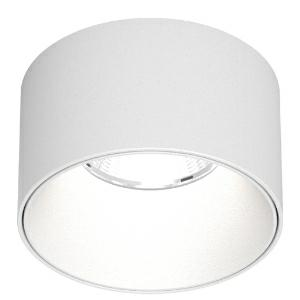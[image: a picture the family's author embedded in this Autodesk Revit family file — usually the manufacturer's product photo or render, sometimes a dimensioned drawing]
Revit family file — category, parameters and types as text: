
# Revit family: invader_semi-on_220-1194
name_source: partatom
category: Lighting Fixtures
units: mm (PartAtom-declared; Revit-internal decimal feet)

## family parameters
Cut with Voids When Loaded = No
Host = Face
Light Source = No
Part Type = Normal
Room Calculation Point = No
Round Connector Dimension = Use Diameter
Shared = No

## types (1)
- 220-1194-H27-W22 (1 x LED, 1043.88 lm, 9.6 W, 2700K)
    Apparent Load = 10 VA
    CIE Flux Codes = 99 100 100 100 67
    Color Rendering = 1A/90…99
    Color Temperature = 2700K
    Default Elevation = 1800 mm
    Description = INVADER SEMI-ON
    Height = 0 mm  [stored 0 ft]
    Lamp = 1 x LED
    Lamp Light Flux = 1043.88 lm
    Lamp Power = 9.6 W
    Lamp count = 1
    Length = 75 mm
    Luminous efficacy = 73 lm/W
    Manufacturer = Prolicht
    ModVariant = No
    Model = 220-1194
    Mounting Place = Ceiling
    Mounting Type = Recessed
    Number of Poles = 1
    OnlyDefault = Yes
    Power Factor = 1
    Product Name = INVADER SEMI-ON
    Product group = Recessed spotlights
    ProductGroupID = 422
    Protection Class = Protection class
    Protection Degree = Degree of protection
    RLX_Detail_Level = 1
    RLX_Emergency_Light_Flux = 0 lm
    RLX_Emergency_Type = 0
    RLX_Emergency_Type_DB = No
    RlxData = <blob elided: 127105 chars, md5=756fdc8c>
    Socket = socket
    Standby Power = 0 W
    System Light Flux = 700 lm
    System Power = 10 W
    Type Comments = LED COLOUR DIR 2700 K (27),BEAMWIDTH Spot (22)
    Type Image = 220-1194.jpg
    URL = http://relux.com
    VarID = 220-1194-h27-w22
    Voltage = 0 V
    Weight = 0.00 kg
    Width = 0 mm  [stored 0 ft]

note: [stored X ft] marks values corroborated as IEEE doubles in the binary element streams (Revit-internal decimal feet)

## geometry (parser evidence)
native form markers: Blend x4, Sweep x12
no freeform markers — native parametric forms only
